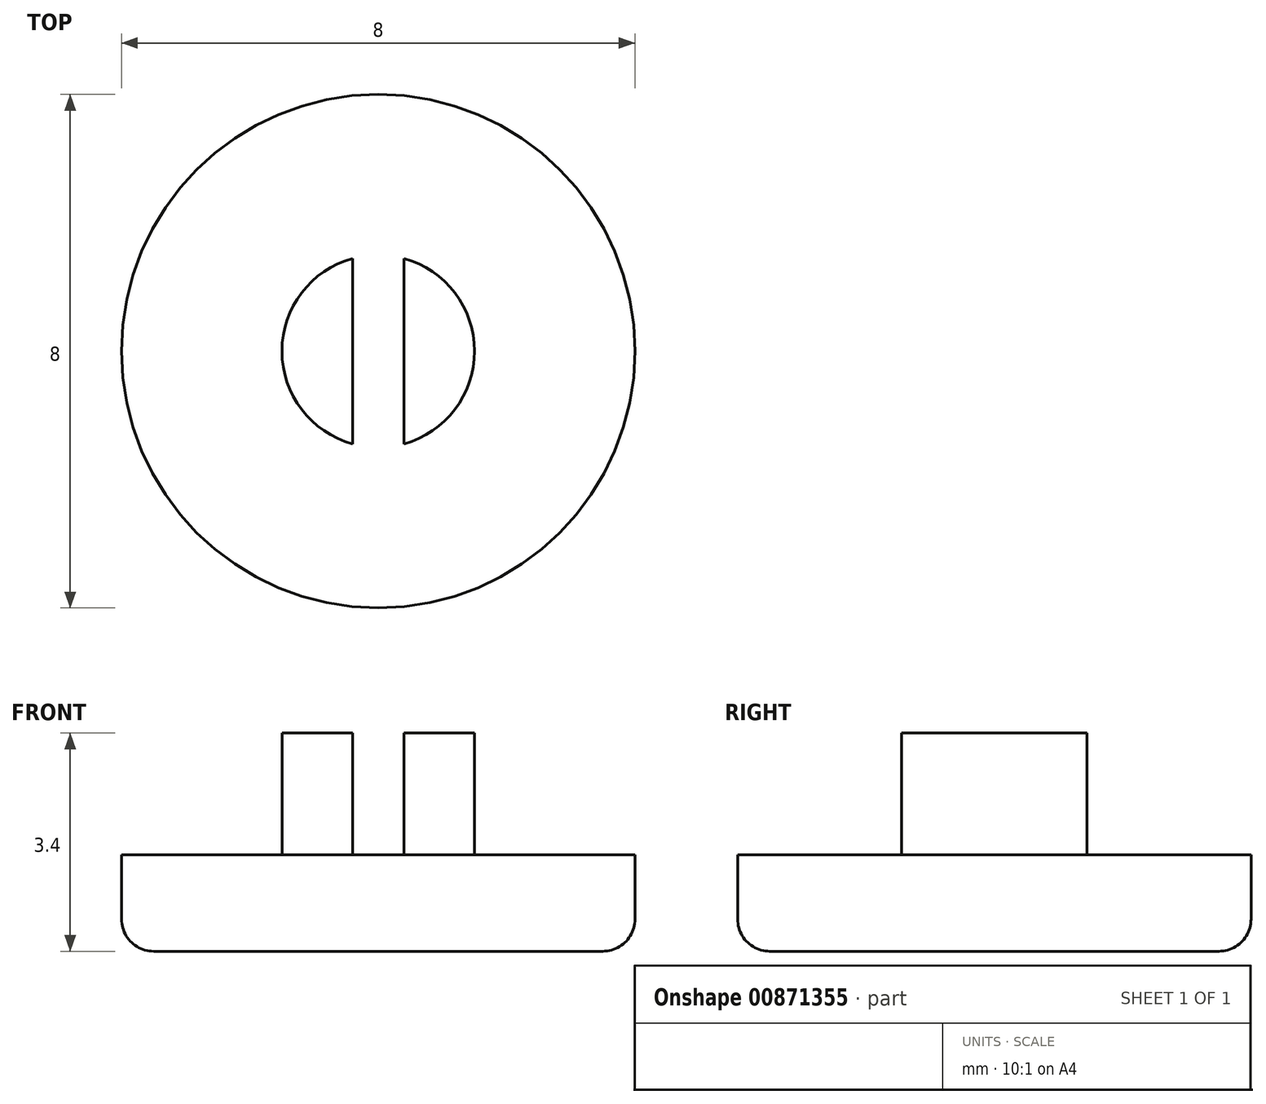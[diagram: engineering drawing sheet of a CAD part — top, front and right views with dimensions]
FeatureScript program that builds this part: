
annotation { "Feature Type Name" : "Feature", "Feature Type Description" : "" }
export const myFeature = defineFeature(function(context is Context, id is Id, definition is map)
    precondition{}
    {
        {
            var Q0;
            Q0=qCreatedBy(makeId("Top.planeOp"),FACE);
            var sketch = newSketch(context, id + "F0", { "sketchPlane" : qUnion([Q0])});
            skCircle(sketch, "E0", {"center": v(0, 0) * mm, "radius": 4 * mm});
            skSolve(sketch);
        }
        {
            var Q0;
            Q0 = qSketchRegion(id + "F0", true);
            extrude(context, id + "F1", {"entities" : qUnion([Q0]), "depth" : 1.5 * mm, "offsetDistance" : 25 * mm});
        }
        {
            var Q0;
            Q0=makeQuery(id+"F1.opExtrude","CAP_FACE",FACE,{"disambiguationData":[OSD([sQuery(id+"F0.wireOp",EDGE,"E0")])],"isStart":false});
            var sketch = newSketch(context, id + "F2", { "sketchPlane" : qUnion([Q0])});
            skCircle(sketch, "E1", {"center": v(0, 0) * mm, "radius": 1.5 * mm});
            skSolve(sketch);
        }
        {
            var Q0;
            Q0=makeQuery(id+"F2.imprint","IMPRINT",FACE,{"disambiguationData":[TD([[makeQuery(id+"F2.imprint","IMPRINT",EDGE,{"derivedFrom":sQuery(id+"F2.wireOp",EDGE,"E1")}),1.0]])]});
            extrude(context, id + "F3", {"entities" : qUnion([Q0]), "operationType" : NewBodyOperationType.ADD, "depth" : 1.9 * mm, "offsetDistance" : 25 * mm});
        }
        {
            var Q0;
            Q0=makeQuery(id+"F3.opExtrude","CAP_FACE",FACE,{"disambiguationData":[OSD([sQuery(id+"F2.wireOp",EDGE,"E1")])],"isStart":false});
            var sketch = newSketch(context, id + "F4", { "sketchPlane" : qUnion([Q0])});
            skLineSegment(sketch, "E2.bottom", {"start": v(0.4, -2.5) * mm, "end": v(-0.4, -2.5) * mm});
            skLineSegment(sketch, "E2.top", {"start": v(0.4, 2.5) * mm, "end": v(-0.4, 2.5) * mm});
            skLineSegment(sketch, "E2.left", {"start": v(0.4, -2.5) * mm, "end": v(0.4, 2.5) * mm});
            skLineSegment(sketch, "E2.right", {"start": v(-0.4, -2.5) * mm, "end": v(-0.4, 2.5) * mm});
            skPoint(sketch, "E2.middle", {"position": v(0, 0) * mm});
            skSolve(sketch);
        }
        {
            var Q0;
            {var subQ0=sQuery(id+"F4.wireOp",EDGE,"E2.left");var subQ1=makeQuery(id+"F3.opExtrude","CAP_EDGE",EDGE,{"disambiguationData":[OSD([sQuery(id+"F2.wireOp",EDGE,"E1")])],"isStart":false});var subQ2=makeQuery(id+"F4.imprint","INTERSECT",VERTEX,{"disambiguationData":[OD(0.0)],"derivedFrom":[subQ1,subQ0]});Q0=makeQuery(id+"F4.imprint","IMPRINT",FACE,{"disambiguationData":[TD([[makeQuery(id+"F4.imprint","IMPRINT",EDGE,{"disambiguationData":[TD([[subQ2,-1.0]])],"derivedFrom":subQ0}),1.0]])]});}
            extrude(context, id + "F5", {"entities" : qUnion([Q0]), "operationType" : NewBodyOperationType.REMOVE, "oppositeDirection" : true, "depth" : 1.9 * mm, "offsetDistance" : 25 * mm});
        }
        {
            var Q0;
            Q0=makeQuery(id+"F5.boolean.opBoolean","MERGE",FACE,{"derivedFrom":[makeQuery(id+"F1.opExtrude","CAP_FACE",FACE,{"disambiguationData":[OSD([sQuery(id+"F0.wireOp",EDGE,"E0")])],"isStart":false}),makeQuery(id+"F5.opExtrude","CAP_FACE",FACE,{"disambiguationData":[OSD([sQuery(id+"F2.wireOp",EDGE,"E1"),sQuery(id+"F4.wireOp",EDGE,"E2.left"),sQuery(id+"F4.wireOp",EDGE,"E2.right")])],"isStart":false})]});
            var sketch = newSketch(context, id + "F6", { "sketchPlane" : qUnion([Q0])});
            skCircle(sketch, "E3", {"center": v(0, 0) * mm, "radius": 1.45 * mm});
            skSolve(sketch);
        }
        {
            var Q0;
            {var subQ0=sQuery(id+"F4.wireOp",EDGE,"E2.left");Q0=makeQuery(id+"F6.imprint","IMPRINT",FACE,{"disambiguationData":[TD([[makeQuery(id+"F6.imprint","IMPRINT",EDGE,{"derivedFrom":makeQuery(id+"F5.boolean.opBoolean","COPY",EDGE,{"derivedFrom":makeQuery(id+"F5.opExtrude","CAP_EDGE",EDGE,{"disambiguationData":[OSD([subQ0])],"isStart":false})})}),-1.0]])]});}
            var Q1;
            {var subQ0=sQuery(id+"F4.wireOp",EDGE,"E2.right");Q1=makeQuery(id+"F6.imprint","IMPRINT",FACE,{"disambiguationData":[TD([[makeQuery(id+"F6.imprint","IMPRINT",EDGE,{"derivedFrom":makeQuery(id+"F5.boolean.opBoolean","COPY",EDGE,{"derivedFrom":makeQuery(id+"F5.opExtrude","CAP_EDGE",EDGE,{"disambiguationData":[OSD([subQ0])],"isStart":false})})}),1.0]])]});}
            var Q2;
            Q2=makeQuery(id+"F6.imprint","IMPRINT",FACE,{"disambiguationData":[TD([[makeQuery(id+"F6.imprint","IMPRINT",EDGE,{"derivedFrom":sQuery(id+"F6.wireOp",EDGE,"KJh1J5F3-LKHd-GiQJ-iAOI-dCW8QJwMHyaR")}),-1.0]])]});
            extrude(context, id + "F7", {"entities" : qUnion([Q0, Q1, Q2]), "operationType" : NewBodyOperationType.ADD, "depth" : 0.3 * mm, "offsetDistance" : 25 * mm});
        }
        {
            var Q0;
            Q0=makeQuery(id+"F1.opExtrude","CAP_FACE",FACE,{"disambiguationData":[OSD([sQuery(id+"F0.wireOp",EDGE,"E0")])],"isStart":true});
            fillet(context, id + "F8", {"entities" : qUnion([Q0]), "radius" : 0.5 * mm, "tangentPropagation" : true, "allowEdgeOverflow" : false});
        }
    });
